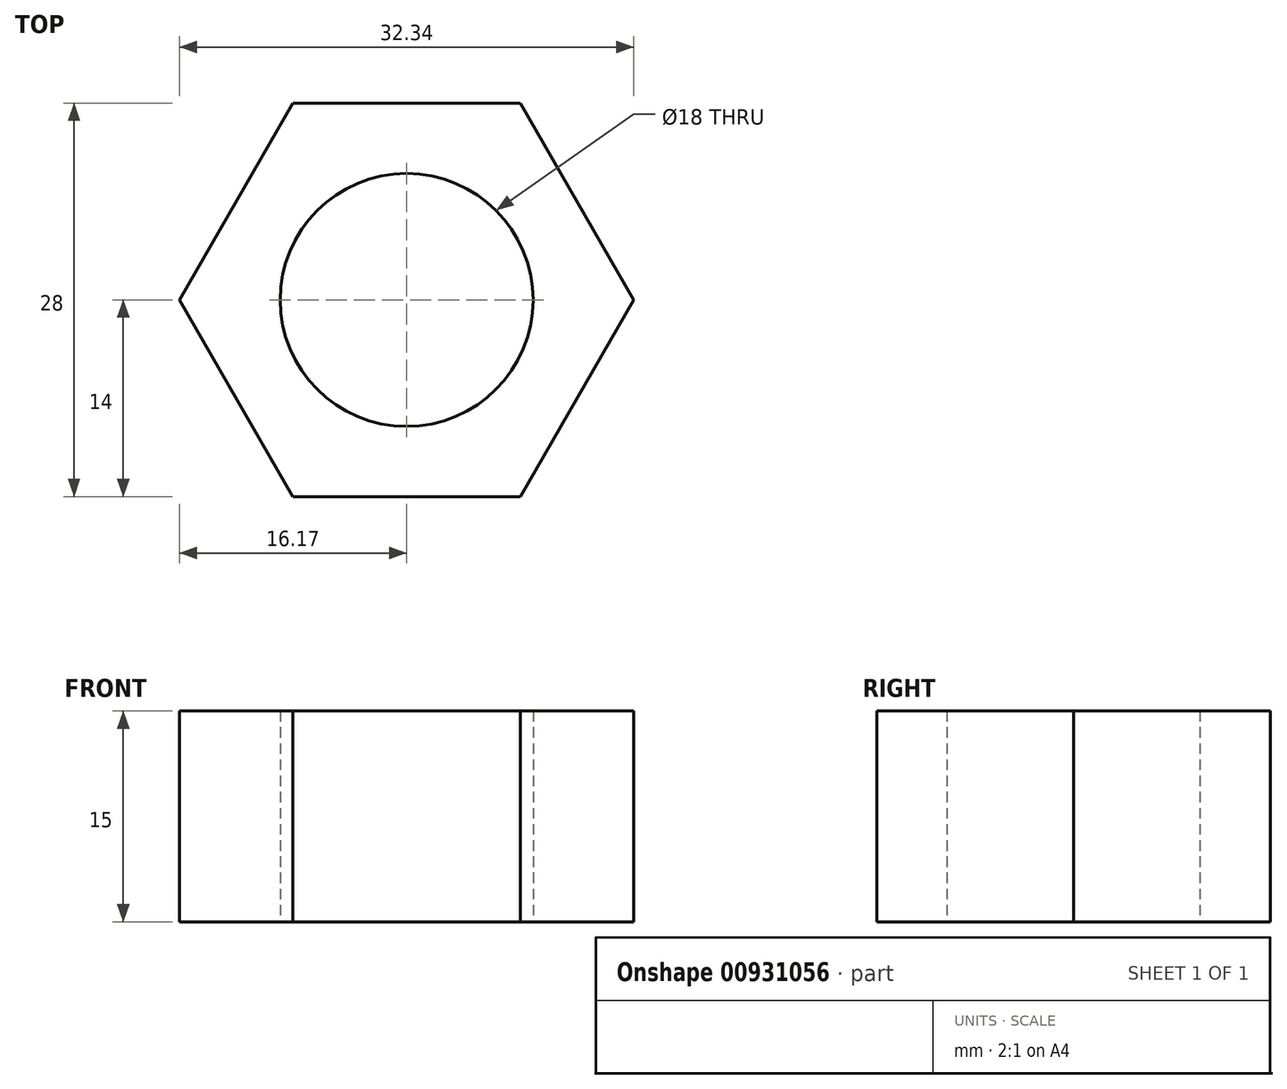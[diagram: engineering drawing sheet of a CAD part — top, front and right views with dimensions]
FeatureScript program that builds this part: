
annotation { "Feature Type Name" : "Feature", "Feature Type Description" : "" }
export const myFeature = defineFeature(function(context is Context, id is Id, definition is map)
    precondition{}
    {
        {
            var Q0;
            Q0=qCreatedBy(makeId("Top.planeOp"),FACE);
            var sketch = newSketch(context, id + "F0", { "sketchPlane" : qUnion([Q0])});
            skCircle(sketch, "E0", {"center": v(0, 0) * mm, "radius": 9 * mm});
            skCircle(sketch, "E1.cCircle", {"center": v(0, 0) * mm, "radius": 14 * mm, "construction": true});
            skLineSegment(sketch, "E1.0", {"start": v(8.08, -14) * mm, "end": v(-8.08, -14) * mm});
            skLineSegment(sketch, "E1.1", {"start": v(-8.08, -14) * mm, "end": v(-16.17, 0) * mm});
            skLineSegment(sketch, "E1.2", {"start": v(-16.17, 0) * mm, "end": v(-8.08, 14) * mm});
            skLineSegment(sketch, "E1.3", {"start": v(-8.08, 14) * mm, "end": v(8.08, 14) * mm});
            skLineSegment(sketch, "E1.4", {"start": v(8.08, 14) * mm, "end": v(16.17, 0) * mm});
            skLineSegment(sketch, "E1.5", {"start": v(16.17, 0) * mm, "end": v(8.08, -14) * mm});
            skPoint(sketch, "E1.0.midPoint", {"position": v(0, -14) * mm});
            skSolve(sketch);
        }
        {
            var Q0;
            Q0=makeQuery(id+"F0.imprint","IMPRINT",FACE,{"disambiguationData":[TD([[makeQuery(id+"F0.imprint","IMPRINT",EDGE,{"derivedFrom":sQuery(id+"F0.wireOp",EDGE,"E0")}),-1.0]])]});
            extrude(context, id + "F1", {"entities" : qUnion([Q0]), "depth" : 15 * mm, "offsetDistance" : 25 * mm});
        }
    });
